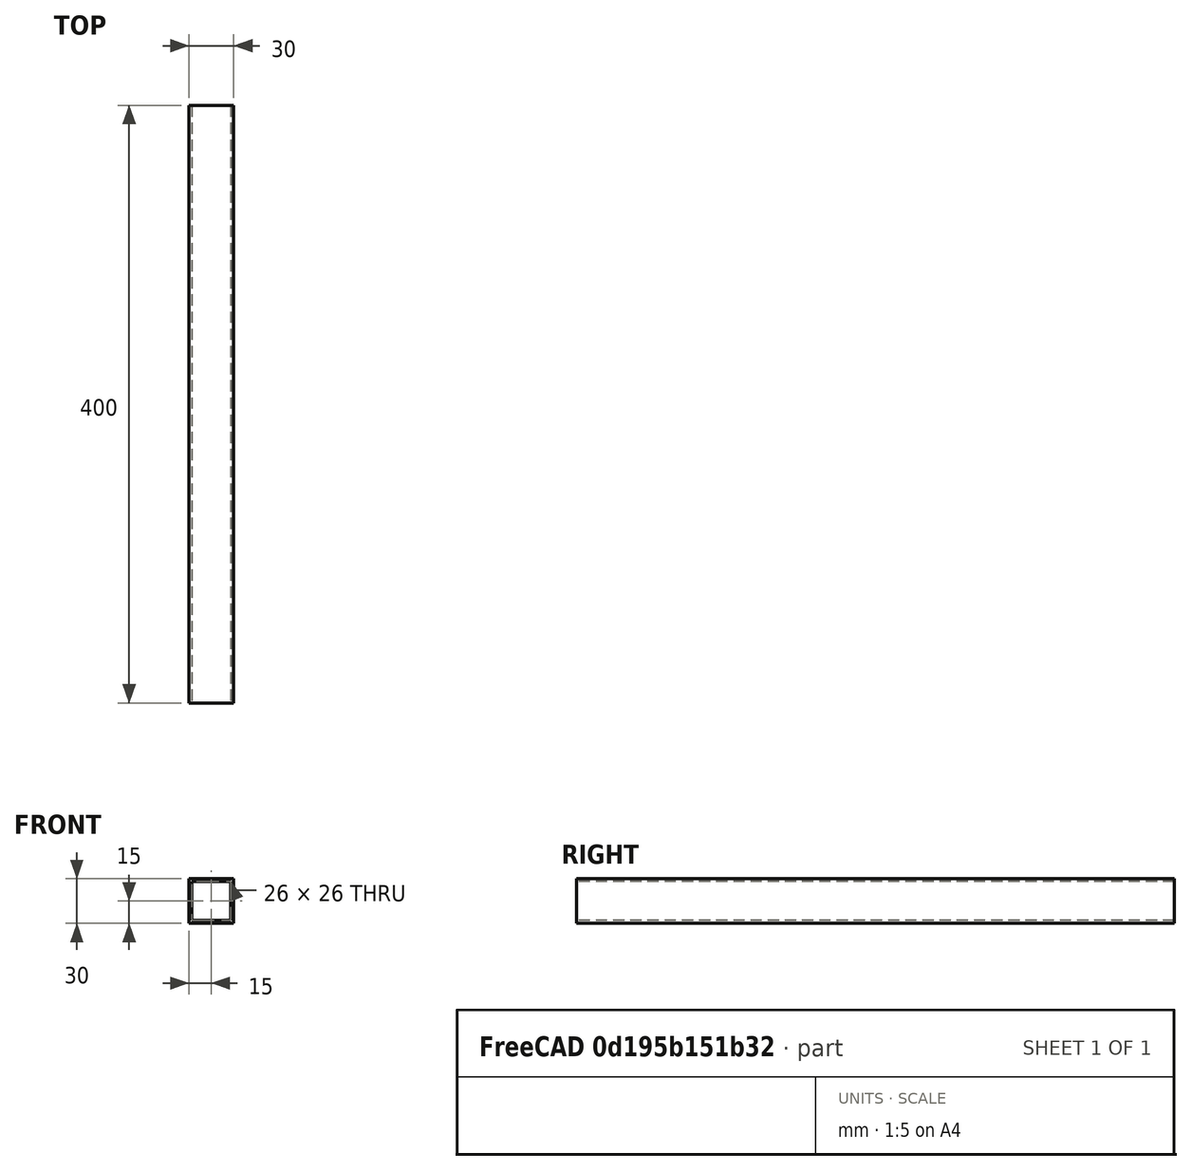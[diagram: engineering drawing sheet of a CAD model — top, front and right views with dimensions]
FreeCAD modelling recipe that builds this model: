
FCSTD DOCUMENT  (FreeCAD 0.20R29177 +426 (Git))
Label: beam_vertical_front
License: All rights reserved
LicenseURL: http://en.wikipedia.org/wiki/All_rights_reserved
objects: Sketcher::SketchObject×1, PartDesign::Pad×1, PartDesign::Body×1
note: 4 computed .brp shape members not serialized (recipe doc carries the construction recipe); baked Part::Feature solids carry a one-line shape summary decoded from their .brp

FEATURE [Sketcher::SketchObject] Sketch
  FullyConstrained = true
  MapMode = 5
  Placement = pos=(0,0,0) rot=(1,0,0;1.5708rad)
  Support = -> [XZ_Plane]
  sketch-geometry (10):
    g0: LineSegment StartX=0 StartY=0 StartZ=0 EndX=30 EndY=0 EndZ=0
    g1: LineSegment StartX=30 StartY=0 StartZ=0 EndX=30 EndY=30 EndZ=0
    g2: LineSegment StartX=30 StartY=30 StartZ=0 EndX=0 EndY=30 EndZ=0
    g3: LineSegment StartX=0 StartY=30 StartZ=0 EndX=0 EndY=0 EndZ=0
    g4: LineSegment StartX=2 StartY=28 StartZ=0 EndX=28 EndY=28 EndZ=0
    g5: LineSegment StartX=28 StartY=28 StartZ=0 EndX=28 EndY=2 EndZ=0
    g6: LineSegment StartX=28 StartY=2 StartZ=0 EndX=2 EndY=2 EndZ=0
    g7: LineSegment StartX=2 StartY=2 StartZ=0 EndX=2 EndY=28 EndZ=0
    g8: LineSegment StartX=0 StartY=0 StartZ=0 EndX=30 EndY=30 EndZ=0
    g9: LineSegment StartX=0 StartY=30 StartZ=0 EndX=30 EndY=0 EndZ=0
  constraints (27):
    c: Coincident(g0,g1)
    c: Coincident(g1,g2)
    c: Coincident(g2,g3)
    c: Coincident(g3,g0)
    c: Horizontal(g0)
    c: Horizontal(g2)
    c: Vertical(g1)
    c: Vertical(g3)
    c: Coincident(g0,g-1)
    c: DistanceX(g2,g2) = 30
    c: Coincident(g4,g5)
    c: Coincident(g5,g6)
    c: Coincident(g6,g7)
    c: Coincident(g7,g4)
    c: Horizontal(g4)
    c: Horizontal(g6)
    c: Vertical(g5)
    c: Vertical(g7)
    c: DistanceY(g4,g1) = 2
    c: Equal(g1,g2)
    c: Equal(g4,g5)
    c: Coincident(g8,g0)
    c: Coincident(g8,g1)
    c: PointOnObject(g4,g8)
    c: Coincident(g9,g2)
    c: Coincident(g9,g0)
    c: PointOnObject(g4,g9)
FEATURE [PartDesign::Pad] Pad
  Direction = (0,-1,-2e-16)
  Length = 400
  Length2 = 10
  Placement = pos=(0,0,0) rot=(1,0,0;1.5708rad)
  Profile = -> Sketch
  ReferenceAxis = -> Sketch [N_Axis]
  Refine = true
  Type = 0
FEATURE [PartDesign::Body] Body
  Group = -> [Sketch,Pad]
  Origin = -> Origin
  Tip = -> Pad
